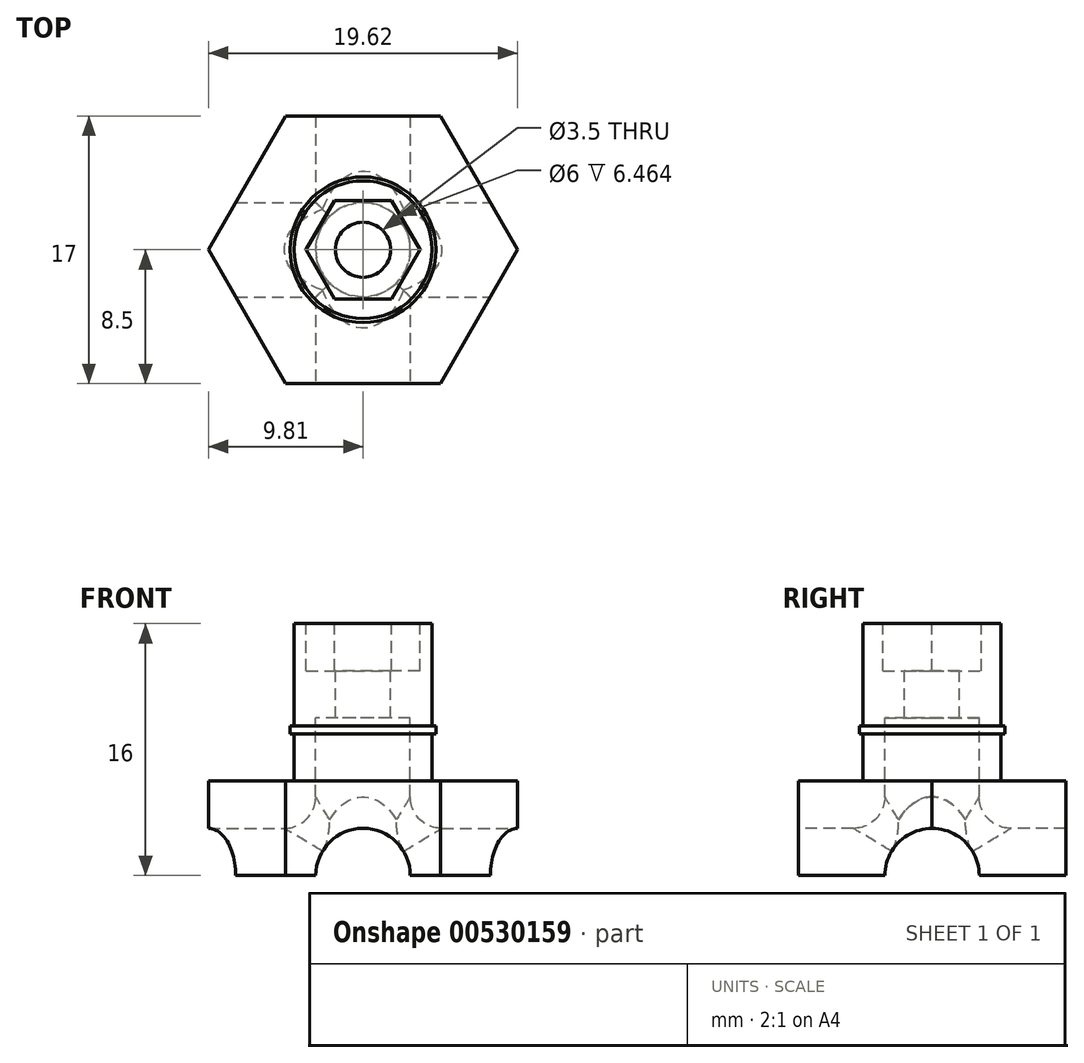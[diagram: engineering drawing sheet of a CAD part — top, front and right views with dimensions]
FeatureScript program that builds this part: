
annotation { "Feature Type Name" : "Feature", "Feature Type Description" : "" }
export const myFeature = defineFeature(function(context is Context, id is Id, definition is map)
    precondition{}
    {
        {
            var Q0;
            Q0=qCreatedBy(makeId("Top.planeOp"),FACE);
            var sketch = newSketch(context, id + "F0", { "sketchPlane" : qUnion([Q0])});
            skCircle(sketch, "E0.cCircle", {"center": v(0, 0) * mm, "radius": 8.5 * mm, "construction": true});
            skLineSegment(sketch, "E0.0", {"start": v(-4.9, 8.5) * mm, "end": v(4.9, 8.5) * mm});
            skLineSegment(sketch, "E0.1", {"start": v(4.9, 8.5) * mm, "end": v(9.81, 0) * mm});
            skLineSegment(sketch, "E0.2", {"start": v(9.81, 0) * mm, "end": v(4.9, -8.5) * mm});
            skLineSegment(sketch, "E0.3", {"start": v(4.9, -8.5) * mm, "end": v(-4.9, -8.5) * mm});
            skLineSegment(sketch, "E0.4", {"start": v(-4.9, -8.5) * mm, "end": v(-9.81, 0) * mm});
            skLineSegment(sketch, "E0.5", {"start": v(-9.81, 0) * mm, "end": v(-4.9, 8.5) * mm});
            skPoint(sketch, "E0.0.midPoint", {"position": v(0, 8.5) * mm});
            skSolve(sketch);
        }
        {
            var Q0;
            Q0=makeQuery(id+"F0.imprint","IMPRINT",FACE,{"disambiguationData":[TD([[makeQuery(id+"F0.imprint","IMPRINT",EDGE,{"derivedFrom":sQuery(id+"F0.wireOp",EDGE,"E0.0")}),-1.0]])]});
            extrude(context, id + "F1", {"entities" : qUnion([Q0]), "depth" : 6 * mm, "offsetDistance" : 25 * mm});
        }
        {
            var Q0;
            Q0=makeQuery(id+"F1.opExtrude","CAP_FACE",FACE,{"disambiguationData":[OSD([sQuery(id+"F0.wireOp",EDGE,"E0.0"),sQuery(id+"F0.wireOp",EDGE,"E0.1"),sQuery(id+"F0.wireOp",EDGE,"E0.2"),sQuery(id+"F0.wireOp",EDGE,"E0.3"),sQuery(id+"F0.wireOp",EDGE,"E0.4"),sQuery(id+"F0.wireOp",EDGE,"E0.5")])],"isStart":false});
            var sketch = newSketch(context, id + "F2", { "sketchPlane" : qUnion([Q0])});
            skCircle(sketch, "E1", {"center": v(0, 0) * mm, "radius": 4.38 * mm});
            skCircle(sketch, "E2", {"center": v(0, 0) * mm, "radius": 4.63 * mm});
            skSolve(sketch);
        }
        {
            var Q0;
            Q0=makeQuery(id+"F2.imprint","IMPRINT",FACE,{"disambiguationData":[TD([[makeQuery(id+"F2.imprint","IMPRINT",EDGE,{"derivedFrom":sQuery(id+"F2.wireOp",EDGE,"E1")}),1.0]])]});
            extrude(context, id + "F3", {"entities" : qUnion([Q0]), "operationType" : NewBodyOperationType.ADD, "depth" : 10 * mm, "offsetDistance" : 25 * mm});
        }
        {
            var Q0;
            Q0=makeQuery(id+"F2.imprint","IMPRINT",FACE,{"disambiguationData":[TD([[makeQuery(id+"F2.imprint","IMPRINT",EDGE,{"derivedFrom":sQuery(id+"F2.wireOp",EDGE,"E1")}),-1.0]])]});
            extrude(context, id + "F4", {"entities" : qUnion([Q0]), "operationType" : NewBodyOperationType.ADD, "depth" : 3.5 * mm, "offsetDistance" : 25 * mm, "hasSecondDirection" : true, "secondDirectionOppositeDirection" : false, "secondDirectionDepth" : 3 * mm});
        }
        {
            var Q0;
            Q0=makeQuery(id+"F3.opExtrude","CAP_FACE",FACE,{"disambiguationData":[OSD([sQuery(id+"F2.wireOp",EDGE,"E1")])],"isStart":false});
            var sketch = newSketch(context, id + "F5", { "sketchPlane" : qUnion([Q0])});
            skCircle(sketch, "E3.cCircle", {"center": v(0, 0) * mm, "radius": 3.12 * mm, "construction": true});
            skLineSegment(sketch, "E3.0", {"start": v(-1.8, 3.12) * mm, "end": v(1.8, 3.12) * mm});
            skLineSegment(sketch, "E3.1", {"start": v(1.8, 3.12) * mm, "end": v(3.6, 0) * mm});
            skLineSegment(sketch, "E3.2", {"start": v(3.6, 0) * mm, "end": v(1.8, -3.12) * mm});
            skLineSegment(sketch, "E3.3", {"start": v(1.8, -3.12) * mm, "end": v(-1.8, -3.13) * mm});
            skLineSegment(sketch, "E3.4", {"start": v(-1.8, -3.13) * mm, "end": v(-3.6, 0) * mm});
            skLineSegment(sketch, "E3.5", {"start": v(-3.6, 0) * mm, "end": v(-1.8, 3.12) * mm});
            skPoint(sketch, "E3.0.midPoint", {"position": v(0, 3.12) * mm});
            skSolve(sketch);
        }
        {
            var Q0;
            Q0=makeQuery(id+"F5.imprint","IMPRINT",FACE,{"disambiguationData":[TD([[makeQuery(id+"F5.imprint","IMPRINT",EDGE,{"derivedFrom":sQuery(id+"F5.wireOp",EDGE,"E3.0")}),-1.0]])]});
            extrude(context, id + "F6", {"entities" : qUnion([Q0]), "operationType" : NewBodyOperationType.REMOVE, "oppositeDirection" : true, "depth" : 3 * mm, "offsetDistance" : 25 * mm});
        }
        {
            var Q0;
            Q0=makeQuery(id+"F3.opExtrude","CAP_FACE",FACE,{"disambiguationData":[OSD([sQuery(id+"F2.wireOp",EDGE,"E1")])],"isStart":false});
            var sketch = newSketch(context, id + "F7", { "sketchPlane" : qUnion([Q0])});
            skCircle(sketch, "E4", {"center": v(0, 0) * mm, "radius": 1.75 * mm});
            skSolve(sketch);
        }
        {
            var Q0;
            Q0=makeQuery(id+"F7.imprint","IMPRINT",FACE,{"disambiguationData":[TD([[makeQuery(id+"F7.imprint","IMPRINT",EDGE,{"derivedFrom":sQuery(id+"F7.wireOp",EDGE,"E4")}),1.0]])]});
            extrude(context, id + "F8", {"entities" : qUnion([Q0]), "operationType" : NewBodyOperationType.REMOVE, "endBound" : BoundingType.THROUGH_ALL, "oppositeDirection" : true, "depth" : 25 * mm, "offsetDistance" : 25 * mm});
        }
        {
            var Q0;
            Q0=makeQuery(id+"F3.opExtrude","CAP_FACE",FACE,{"disambiguationData":[OSD([sQuery(id+"F2.wireOp",EDGE,"E1")])],"isStart":false});
            var sketch = newSketch(context, id + "F9", { "sketchPlane" : qUnion([Q0])});
            skCircle(sketch, "E5", {"center": v(0, 0) * mm, "radius": 3 * mm});
            skSolve(sketch);
        }
        {
            var Q0;
            Q0 = qSketchRegion(id + "F9", true);
            var Q1;
            Q1=makeQuery(id+"F1.opExtrude","CAP_FACE",FACE,{"disambiguationData":[OSD([sQuery(id+"F0.wireOp",EDGE,"E0.0"),sQuery(id+"F0.wireOp",EDGE,"E0.1"),sQuery(id+"F0.wireOp",EDGE,"E0.2"),sQuery(id+"F0.wireOp",EDGE,"E0.3"),sQuery(id+"F0.wireOp",EDGE,"E0.4"),sQuery(id+"F0.wireOp",EDGE,"E0.5")])],"isStart":true});
            extrude(context, id + "F10", {"entities" : qUnion([Q0]), "operationType" : NewBodyOperationType.REMOVE, "endBound" : BoundingType.UP_TO_SURFACE, "oppositeDirection" : true, "depth" : 25 * mm, "endBoundEntityFace" : qUnion([Q1]), "offsetDistance" : 25 * mm, "hasSecondDirection" : true, "secondDirectionOppositeDirection" : true, "secondDirectionDepth" : 6 * mm});
        }
        {
            var Q0;
            Q0=qCreatedBy(makeId("Front.planeOp"),FACE);
            var sketch = newSketch(context, id + "F11", { "sketchPlane" : qUnion([Q0])});
            skCircle(sketch, "E6", {"center": v(0, 0) * mm, "radius": 3 * mm});
            skSolve(sketch);
        }
        {
            var Q0;
            Q0 = qSketchRegion(id + "F11", true);
            var Q1;
            Q1=makeQuery(id+"F1.opExtrude","SWEPT_FACE",FACE,{"disambiguationData":[OSD([sQuery(id+"F0.wireOp",EDGE,"E0.0")])]});
            var Q2;
            Q2=makeQuery(id+"F1.opExtrude","SWEPT_FACE",FACE,{"disambiguationData":[OSD([sQuery(id+"F0.wireOp",EDGE,"E0.3")])]});
            extrude(context, id + "F12", {"entities" : qUnion([Q0]), "operationType" : NewBodyOperationType.REMOVE, "oppositeDirection" : true, "depth" : 25 * mm, "endBoundEntityFace" : qUnion([Q1]), "offsetDistance" : 25 * mm, "symmetric" : true});
        }
        {
            var Q0;
            Q0=qCreatedBy(makeId("Right.planeOp"),FACE);
            var sketch = newSketch(context, id + "F13", { "sketchPlane" : qUnion([Q0])});
            skCircle(sketch, "E7", {"center": v(0, 0) * mm, "radius": 3 * mm});
            skSolve(sketch);
        }
        {
            var Q0;
            Q0 = qSketchRegion(id + "F13", true);
            extrude(context, id + "F14", {"entities" : qUnion([Q0]), "operationType" : NewBodyOperationType.REMOVE, "oppositeDirection" : true, "depth" : 25 * mm, "offsetDistance" : 25 * mm, "symmetric" : true});
        }
        {
            var Q0;
            Q0=makeQuery(id+"F14.boolean.opBoolean","SPLIT",EDGE,{"disambiguationData":[OD(1.0)],"derivedFrom":makeQuery(id+"F12.boolean.opBoolean","INTERSECT",EDGE,{"derivedFrom":[makeQuery(id+"F10.boolean.opBoolean","COPY",FACE,{"derivedFrom":makeQuery(id+"F10.opExtrude","SWEPT_FACE",FACE,{"disambiguationData":[OSD([sQuery(id+"F9.wireOp",EDGE,"E5")])]})}),makeQuery(id+"F12.opExtrude","SWEPT_FACE",FACE,{"disambiguationData":[OSD([sQuery(id+"F11.wireOp",EDGE,"E6")])]})]})});
            var Q1;
            Q1=makeQuery(id+"F14.boolean.opBoolean","INTERSECT",EDGE,{"disambiguationData":[OD(1.0)],"derivedFrom":[makeQuery(id+"F10.boolean.opBoolean","COPY",FACE,{"derivedFrom":makeQuery(id+"F10.opExtrude","SWEPT_FACE",FACE,{"disambiguationData":[OSD([sQuery(id+"F9.wireOp",EDGE,"E5")])]})}),makeQuery(id+"F14.opExtrude","SWEPT_FACE",FACE,{"disambiguationData":[OSD([sQuery(id+"F13.wireOp",EDGE,"E7")])]})]});
            var Q2;
            Q2=makeQuery(id+"F14.boolean.opBoolean","SPLIT",EDGE,{"disambiguationData":[OD(0.0)],"derivedFrom":makeQuery(id+"F12.boolean.opBoolean","INTERSECT",EDGE,{"derivedFrom":[makeQuery(id+"F10.boolean.opBoolean","COPY",FACE,{"derivedFrom":makeQuery(id+"F10.opExtrude","SWEPT_FACE",FACE,{"disambiguationData":[OSD([sQuery(id+"F9.wireOp",EDGE,"E5")])]})}),makeQuery(id+"F12.opExtrude","SWEPT_FACE",FACE,{"disambiguationData":[OSD([sQuery(id+"F11.wireOp",EDGE,"E6")])]})]})});
            var Q3;
            Q3=makeQuery(id+"F14.boolean.opBoolean","INTERSECT",EDGE,{"disambiguationData":[OD(0.0)],"derivedFrom":[makeQuery(id+"F10.boolean.opBoolean","COPY",FACE,{"derivedFrom":makeQuery(id+"F10.opExtrude","SWEPT_FACE",FACE,{"disambiguationData":[OSD([sQuery(id+"F9.wireOp",EDGE,"E5")])]})}),makeQuery(id+"F14.opExtrude","SWEPT_FACE",FACE,{"disambiguationData":[OSD([sQuery(id+"F13.wireOp",EDGE,"E7")])]})]});
            fillet(context, id + "F15", {"entities" : qUnion([Q0, Q1, Q2, Q3]), "tangentPropagation" : true, "radius" : 2 * mm, "defaultsChanged" : false, "vertexSettings" : [], "allowEdgeOverflow" : false});
        }
    });
